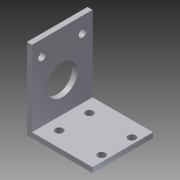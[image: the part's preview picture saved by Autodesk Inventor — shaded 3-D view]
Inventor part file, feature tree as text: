
AUTODESK INVENTOR PART (.ipt)
format: ipt  version: 2013 (Build 170138000, 138)  size: 118,272 bytes
history: native  units: in
note: dims shown in document units (in); Inventor stores cm internally (conversion verified against a paired STEP export)
features: extrude x3, sketch x3
ambient origin geometry x8: Origin, YZ Plane, XZ Plane, XY Plane, X Axis, Y Axis, Z Axis, Center Point
bodies: Solid1 (feature_tree)
feature tree (6):
  extrude  "Extrusion1"  Depth=2.0in
  extrude  "Extrusion2"  Depth=1.5in TaperAngle=0.0deg
  extrude  "Extrusion3"  Depth=0.375in
  sketch  "Sketch1"  dims[d0=2.0in d1=2.0in]
  sketch  "Sketch2"  dims[d2=0.125in d3=1.5in d4=0.0in]
  sketch  "Sketch3"  dims[d5=1.0in d6=0.375in d7=0.1875in d8=0.1875in d9=1.5in d10=0.0in d11=0.75in d12=0.875in d13=0.75in d17=0.1875in d18=0.425in d19=1.0in d20=0.0in d21=1.625in d22=0.7874in d24=1.05in d25=0.3937in d27=1.0in]
